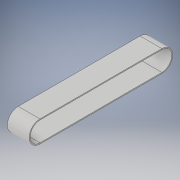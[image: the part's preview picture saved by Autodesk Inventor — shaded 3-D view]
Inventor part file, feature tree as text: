
AUTODESK INVENTOR PART (.ipt)
format: ipt  version: 2019 (Build 230136000, 136)  size: 114,176 bytes
history: native  units: mm
features: extrude x2, sketch x2, other x1
ambient origin geometry x8: Origin, YZ Plane, XZ Plane, XY Plane, X Axis, Y Axis, Z Axis, Center Point
bodies: Body1 (feature_tree)
feature tree (5):
  other  "ソリッド1"
  extrude  "押し出し1"  Depth=224.336mm
  extrude  "押し出し2"  Depth=224.336mm
  sketch  "スケッチ1"
  sketch  "スケッチ2"
